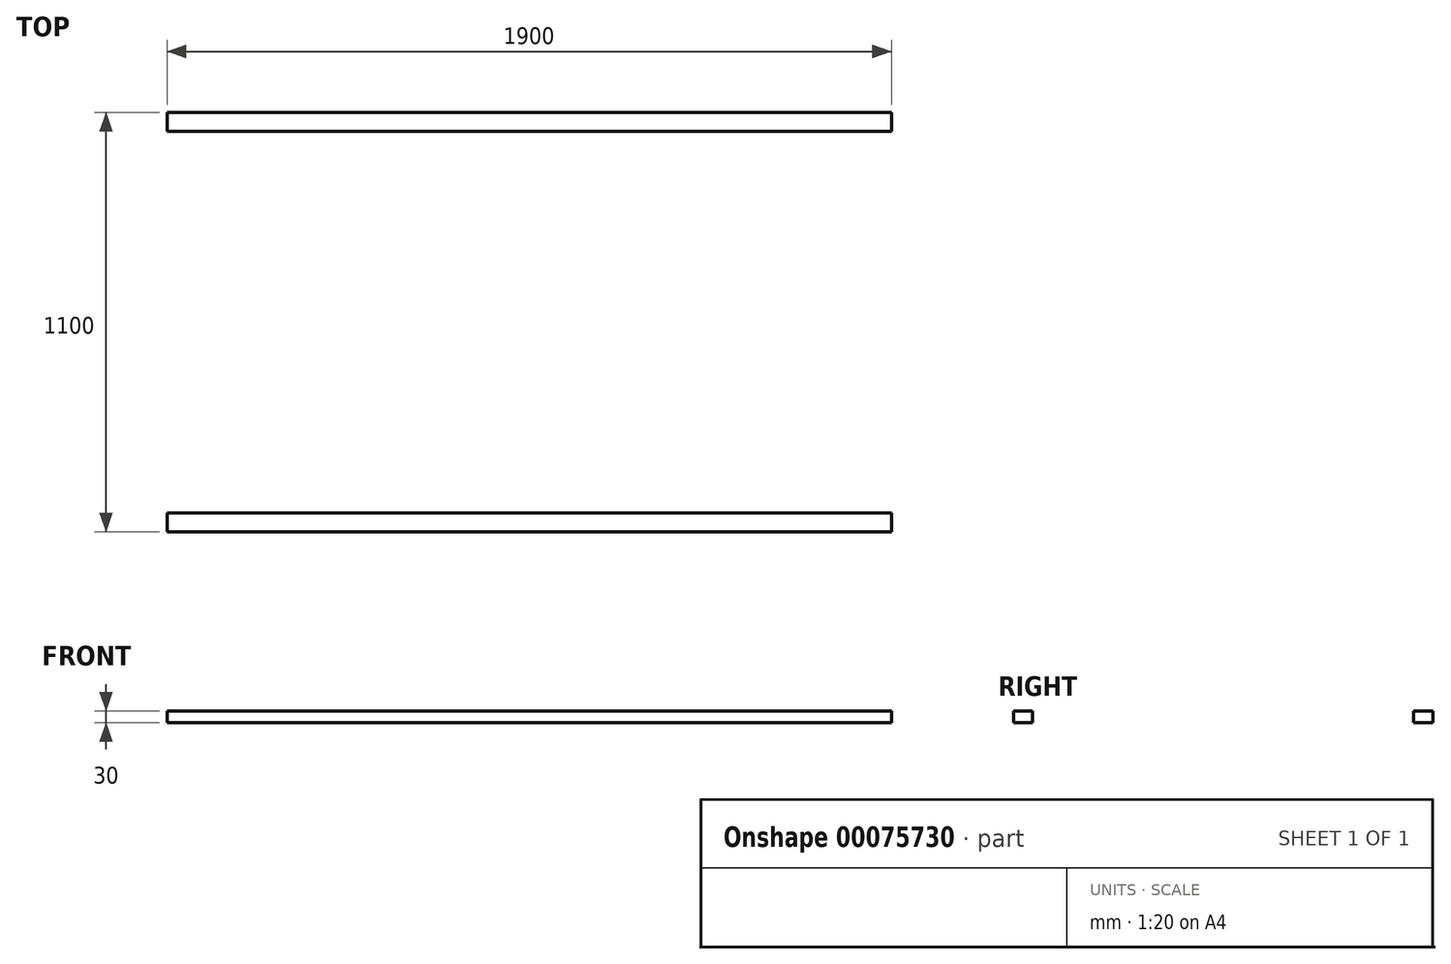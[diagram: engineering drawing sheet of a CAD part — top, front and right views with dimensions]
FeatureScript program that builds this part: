
annotation { "Feature Type Name" : "Feature", "Feature Type Description" : "" }
export const myFeature = defineFeature(function(context is Context, id is Id, definition is map)
    precondition{}
    {
        {
            var Q0;
            Q0=qCreatedBy(makeId("Top.planeOp"),FACE);
            var sketch = newSketch(context, id + "F0", { "sketchPlane" : qUnion([Q0])});
            skLineSegment(sketch, "E0.bottom", {"start": v(-861.44, 546.2) * mm, "end": v(1038.56, 546.2) * mm});
            skLineSegment(sketch, "E0.top", {"start": v(-861.44, 496.2) * mm, "end": v(1038.56, 496.2) * mm});
            skLineSegment(sketch, "E0.left", {"start": v(-861.44, 546.2) * mm, "end": v(-861.44, 496.2) * mm});
            skLineSegment(sketch, "E0.right", {"start": v(1038.56, 546.2) * mm, "end": v(1038.56, 496.2) * mm});
            skLineSegment(sketch, "E1.bottom", {"start": v(-861.44, 496.2) * mm, "end": v(-811.44, 496.2) * mm});
            skLineSegment(sketch, "E1.top", {"start": v(-861.44, -503.8) * mm, "end": v(-811.44, -503.8) * mm});
            skLineSegment(sketch, "E1.left", {"start": v(-861.44, 496.2) * mm, "end": v(-861.44, -503.8) * mm});
            skLineSegment(sketch, "E1.right", {"start": v(-811.44, 496.2) * mm, "end": v(-811.44, -503.8) * mm});
            skLineSegment(sketch, "E2.bottom", {"start": v(-861.44, -503.8) * mm, "end": v(1038.56, -503.8) * mm});
            skLineSegment(sketch, "E2.top", {"start": v(-861.44, -553.8) * mm, "end": v(1038.56, -553.8) * mm});
            skLineSegment(sketch, "E2.left", {"start": v(-861.44, -503.8) * mm, "end": v(-861.44, -553.8) * mm});
            skLineSegment(sketch, "E2.right", {"start": v(1038.56, -503.8) * mm, "end": v(1038.56, -553.8) * mm});
            skLineSegment(sketch, "E3.bottom", {"start": v(1038.56, 496.2) * mm, "end": v(988.56, 496.2) * mm});
            skLineSegment(sketch, "E3.top", {"start": v(1038.56, -503.8) * mm, "end": v(988.56, -503.8) * mm});
            skLineSegment(sketch, "E3.left", {"start": v(1038.56, 496.2) * mm, "end": v(1038.56, -503.8) * mm});
            skLineSegment(sketch, "E3.right", {"start": v(988.56, 496.2) * mm, "end": v(988.56, -503.8) * mm});
            skLineSegment(sketch, "E4.bottom", {"start": v(238.56, 496.2) * mm, "end": v(288.56, 496.2) * mm});
            skLineSegment(sketch, "E4.top", {"start": v(238.56, -503.8) * mm, "end": v(288.56, -503.8) * mm});
            skLineSegment(sketch, "E4.left", {"start": v(238.56, 496.2) * mm, "end": v(238.56, -503.8) * mm});
            skLineSegment(sketch, "E4.right", {"start": v(288.56, 496.2) * mm, "end": v(288.56, -503.8) * mm});
            skSolve(sketch);
        }
        {
            var Q0;
            Q0=makeQuery(id+"F0.imprint","IMPRINT",FACE,{"disambiguationData":[TD([[makeQuery(id+"F0.imprint","IMPRINT",EDGE,{"derivedFrom":sQuery(id+"F0.wireOp",EDGE,"E1.bottom")}),-1.0]])]});
            var Q1;
            Q1=makeQuery(id+"F0.imprint","IMPRINT",FACE,{"disambiguationData":[TD([[makeQuery(id+"F0.imprint","IMPRINT",EDGE,{"derivedFrom":sQuery(id+"F0.wireOp",EDGE,"E3.bottom")}),1.0]])]});
            var Q2;
            Q2=makeQuery(id+"F0.imprint","IMPRINT",FACE,{"disambiguationData":[TD([[makeQuery(id+"F0.imprint","IMPRINT",EDGE,{"derivedFrom":sQuery(id+"F0.wireOp",EDGE,"E4.bottom")}),-1.0]])]});
            var Q3;
            Q3=makeQuery(id+"F0.imprint","IMPRINT",FACE,{"disambiguationData":[TD([[makeQuery(id+"F0.imprint","IMPRINT",EDGE,{"derivedFrom":sQuery(id+"F0.wireOp",EDGE,"E2.top")}),1.0]])]});
            var Q4;
            Q4=makeQuery(id+"F0.imprint","IMPRINT",FACE,{"disambiguationData":[TD([[makeQuery(id+"F0.imprint","IMPRINT",EDGE,{"derivedFrom":sQuery(id+"F0.wireOp",EDGE,"E0.bottom")}),-1.0]])]});
            extrude(context, id + "F1", {"entities" : qUnion([Q0, Q1, Q2, Q3, Q4]), "depth" : 30 * mm});
        }
    });
